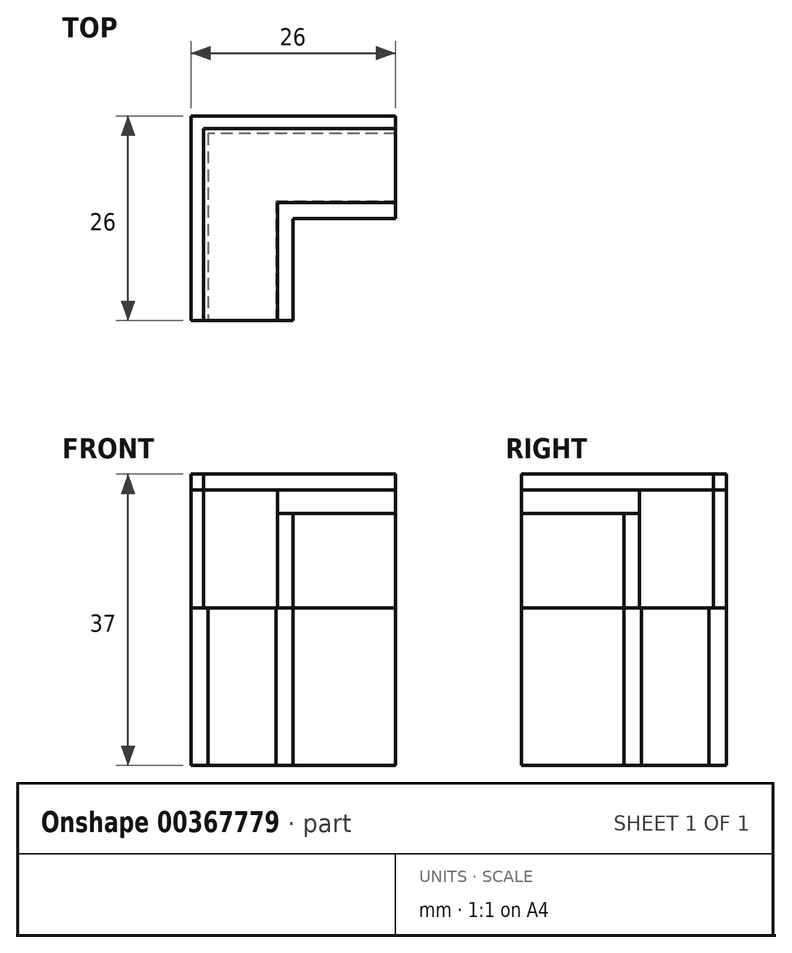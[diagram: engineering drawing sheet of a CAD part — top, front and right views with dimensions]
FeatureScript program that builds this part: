
annotation { "Feature Type Name" : "Feature", "Feature Type Description" : "" }
export const myFeature = defineFeature(function(context is Context, id is Id, definition is map)
    precondition{}
    {
        {
            var Q0;
            Q0=qCreatedBy(makeId("Top.planeOp"),FACE);
            var sketch = newSketch(context, id + "F0", { "sketchPlane" : qUnion([Q0])});
            skLineSegment(sketch, "E0.top", {"start": v(0, -13) * mm, "end": v(-13, -13) * mm});
            skLineSegment(sketch, "E0.left", {"start": v(0, 0) * mm, "end": v(0, -13) * mm});
            skLineSegment(sketch, "E0.right", {"start": v(-13, 0) * mm, "end": v(-13, -13) * mm});
            skLineSegment(sketch, "E1.top", {"start": v(0, 13) * mm, "end": v(-13, 13) * mm});
            skLineSegment(sketch, "E1.right", {"start": v(-13, 0) * mm, "end": v(-13, 13) * mm});
            skLineSegment(sketch, "E2.bottom", {"start": v(0, 0) * mm, "end": v(13, 0) * mm});
            skLineSegment(sketch, "E2.top", {"start": v(0, 13) * mm, "end": v(13, 13) * mm});
            skLineSegment(sketch, "E2.right", {"start": v(13, 0) * mm, "end": v(13, 13) * mm});
            skLineSegment(sketch, "E3.0", {"start": v(0, 10.8) * mm, "end": v(13, 10.8) * mm});
            skLineSegment(sketch, "E3.1", {"start": v(0, 10.8) * mm, "end": v(-10.8, 10.8) * mm});
            skLineSegment(sketch, "E3.2", {"start": v(-10.8, 0) * mm, "end": v(-10.8, 10.8) * mm});
            skLineSegment(sketch, "E3.3", {"start": v(-10.8, 0) * mm, "end": v(-10.8, -13) * mm});
            skLineSegment(sketch, "E4.0", {"start": v(-2.2, 2.2) * mm, "end": v(-2.2, -13) * mm});
            skLineSegment(sketch, "E4.1", {"start": v(-2.2, 2.2) * mm, "end": v(13, 2.2) * mm});
            skLineSegment(sketch, "E5.0", {"start": v(-2, 2) * mm, "end": v(-2, -13) * mm});
            skLineSegment(sketch, "E5.1", {"start": v(-2, 2) * mm, "end": v(13, 2) * mm});
            skLineSegment(sketch, "E6.0", {"start": v(-11.4, 0) * mm, "end": v(-11.4, -13) * mm});
            skLineSegment(sketch, "E6.1", {"start": v(-11.4, 0) * mm, "end": v(-11.4, 11.4) * mm});
            skLineSegment(sketch, "E6.2", {"start": v(0, 11.4) * mm, "end": v(-11.4, 11.4) * mm});
            skLineSegment(sketch, "E6.3", {"start": v(0, 11.4) * mm, "end": v(13, 11.4) * mm});
            skSolve(sketch);
        }
        {
            var Q0;
            {var subQ1=sQuery(id+"F0.wireOp",EDGE,"E0.right");Q0=makeQuery(id+"F0.imprint","IMPRINT",FACE,{"disambiguationData":[TD([[makeQuery(id+"F0.imprint","IMPRINT",EDGE,{"derivedFrom":subQ1}),1.0]])]});}
            var Q1;
            {var subQ1=sQuery(id+"F0.wireOp",EDGE,"E4.0");Q1=makeQuery(id+"F0.imprint","IMPRINT",FACE,{"disambiguationData":[TD([[makeQuery(id+"F0.imprint","IMPRINT",EDGE,{"derivedFrom":subQ1}),1.0]])]});}
            var Q2;
            {var subQ1=sQuery(id+"F0.wireOp",EDGE,"E0.left");Q2=makeQuery(id+"F0.imprint","IMPRINT",FACE,{"disambiguationData":[TD([[makeQuery(id+"F0.imprint","IMPRINT",EDGE,{"derivedFrom":subQ1}),-1.0]])]});}
            var Q3;
            {var subQ0=sQuery(id+"F0.wireOp",EDGE,"E3.0");Q3=makeQuery(id+"F0.imprint","IMPRINT",FACE,{"disambiguationData":[TD([[makeQuery(id+"F0.imprint","IMPRINT",EDGE,{"derivedFrom":subQ0}),1.0]])]});}
            extrude(context, id + "F1", {"entities" : qUnion([Q0, Q1, Q2, Q3]), "depth" : -20 * mm});
        }
        {
            var Q0;
            {var subQ1=sQuery(id+"F0.wireOp",EDGE,"E0.left");Q0=makeQuery(id+"F0.imprint","IMPRINT",FACE,{"disambiguationData":[TD([[makeQuery(id+"F0.imprint","IMPRINT",EDGE,{"derivedFrom":subQ1}),-1.0]])]});}
            extrude(context, id + "F2", {"entities" : qUnion([Q0]), "depth" : 12 * mm});
        }
        {
            var Q0;
            {var subQ0=sQuery(id+"F0.wireOp",EDGE,"E0.right");Q0=makeQuery(id+"F0.imprint","IMPRINT",FACE,{"disambiguationData":[TD([[makeQuery(id+"F0.imprint","IMPRINT",EDGE,{"derivedFrom":subQ0}),1.0]])]});}
            extrude(context, id + "F3", {"entities" : qUnion([Q0]), "depth" : 17 * mm});
        }
        {
            var Q0;
            {var subQ0=sQuery(id+"F0.wireOp",EDGE,"E0.right");Q0=makeQuery(id+"F0.imprint","IMPRINT",FACE,{"disambiguationData":[TD([[makeQuery(id+"F0.imprint","IMPRINT",EDGE,{"derivedFrom":subQ0}),1.0]])]});}
            var Q1;
            {var subQ0=sQuery(id+"F0.wireOp",EDGE,"E3.0");Q1=makeQuery(id+"F0.imprint","IMPRINT",FACE,{"disambiguationData":[TD([[makeQuery(id+"F0.imprint","IMPRINT",EDGE,{"derivedFrom":subQ0}),1.0]])]});}
            var Q2;
            {var subQ0=sQuery(id+"F0.wireOp",EDGE,"E3.0");Q2=makeQuery(id+"F0.imprint","IMPRINT",FACE,{"disambiguationData":[TD([[makeQuery(id+"F0.imprint","IMPRINT",EDGE,{"derivedFrom":subQ0}),-1.0]])]});}
            var Q3;
            {var subQ0=sQuery(id+"F0.wireOp",EDGE,"E4.0");Q3=makeQuery(id+"F0.imprint","IMPRINT",FACE,{"disambiguationData":[TD([[makeQuery(id+"F0.imprint","IMPRINT",EDGE,{"derivedFrom":subQ0}),1.0]])]});}
            extrude(context, id + "F4", {"entities" : qUnion([Q0, Q1, Q2, Q3]), "depth" : 15 * mm});
        }
    });
